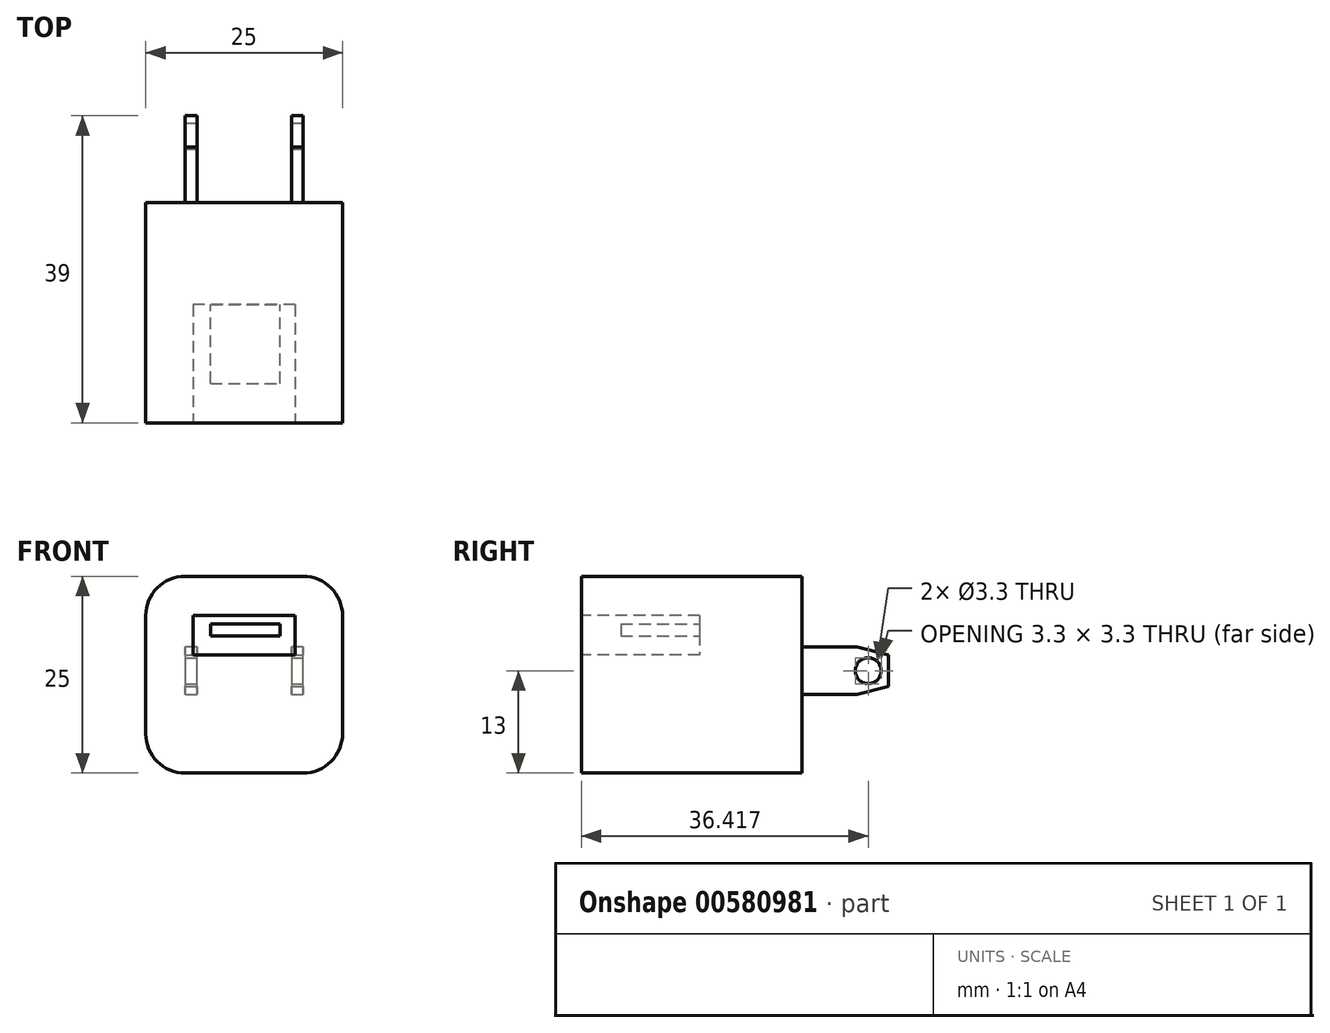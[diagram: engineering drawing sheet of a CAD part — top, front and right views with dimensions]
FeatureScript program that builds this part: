
annotation { "Feature Type Name" : "Feature", "Feature Type Description" : "" }
export const myFeature = defineFeature(function(context is Context, id is Id, definition is map)
    precondition{}
    {
        {
            var Q0;
            Q0=qCreatedBy(makeId("Front.planeOp"),FACE);
            var sketch = newSketch(context, id + "F0", { "sketchPlane" : qUnion([Q0])});
            skLineSegment(sketch, "E0.bottom", {"start": v(12.5, 12.5) * mm, "end": v(-12.5, 12.5) * mm});
            skLineSegment(sketch, "E0.top", {"start": v(12.5, -12.5) * mm, "end": v(-12.5, -12.5) * mm});
            skLineSegment(sketch, "E0.left", {"start": v(12.5, 12.5) * mm, "end": v(12.5, -12.5) * mm});
            skLineSegment(sketch, "E0.right", {"start": v(-12.5, 12.5) * mm, "end": v(-12.5, -12.5) * mm});
            skPoint(sketch, "E0.middle", {"position": v(0, 0) * mm});
            skSolve(sketch);
        }
        {
            var Q0;
            Q0=makeQuery(id+"F0.imprint","IMPRINT",FACE,{"disambiguationData":[TD([[makeQuery(id+"F0.imprint","IMPRINT",EDGE,{"derivedFrom":sQuery(id+"F0.wireOp",EDGE,"E0.bottom")}),1.0]])]});
            extrude(context, id + "F1", {"entities" : qUnion([Q0]), "endBound" : BoundingType.SYMMETRIC, "oppositeDirection" : true, "depth" : 28 * mm, "offsetDistance" : 25 * mm});
        }
        {
            var Q0;
            Q0=makeQuery(id+"F1.opExtrude","CAP_FACE",FACE,{"disambiguationData":[OSD([sQuery(id+"F0.wireOp",EDGE,"E0.bottom"),sQuery(id+"F0.wireOp",EDGE,"E0.top"),sQuery(id+"F0.wireOp",EDGE,"E0.left"),sQuery(id+"F0.wireOp",EDGE,"E0.right")])],"isStart":true});
            var sketch = newSketch(context, id + "F2", { "sketchPlane" : qUnion([Q0])});
            skPoint(sketch, "E1.endSnap0", {"position": v(0, -12.5) * mm});
            skLineSegment(sketch, "E2", {"start": v(0, 2.5) * mm, "end": v(-6.5, 2.5) * mm});
            skLineSegment(sketch, "E3", {"start": v(-6.5, 2.5) * mm, "end": v(-6.5, 7.5) * mm});
            skLineSegment(sketch, "E4", {"start": v(-6.5, 7.5) * mm, "end": v(6.5, 7.5) * mm});
            skLineSegment(sketch, "E5", {"start": v(6.5, 7.5) * mm, "end": v(6.5, 2.5) * mm});
            skLineSegment(sketch, "E6", {"start": v(6.5, 2.5) * mm, "end": v(0, 2.5) * mm});
            skSolve(sketch);
        }
        {
            var Q0;
            Q0=makeQuery(id+"F2.imprint","IMPRINT",FACE,{"disambiguationData":[TD([[makeQuery(id+"F2.imprint","IMPRINT",EDGE,{"derivedFrom":sQuery(id+"F2.wireOp",EDGE,"E2")}),-1.0]])]});
            extrude(context, id + "F3", {"entities" : qUnion([Q0]), "operationType" : NewBodyOperationType.REMOVE, "oppositeDirection" : true, "depth" : 15 * mm, "offsetDistance" : 25 * mm});
        }
        {
            var Q0;
            Q0=makeQuery(id+"F1.opExtrude","CAP_FACE",FACE,{"disambiguationData":[OSD([sQuery(id+"F0.wireOp",EDGE,"E0.bottom"),sQuery(id+"F0.wireOp",EDGE,"E0.top"),sQuery(id+"F0.wireOp",EDGE,"E0.left"),sQuery(id+"F0.wireOp",EDGE,"E0.right")])],"isStart":false});
            var sketch = newSketch(context, id + "F4", { "sketchPlane" : qUnion([Q0])});
            skLineSegment(sketch, "E7", {"start": v(-7.5, -2.5) * mm, "end": v(-7.5, 3.5) * mm});
            skLineSegment(sketch, "E8", {"start": v(-7.5, 3.5) * mm, "end": v(-6, 3.5) * mm});
            skLineSegment(sketch, "E9", {"start": v(-6, 3.5) * mm, "end": v(-6, -2.5) * mm});
            skLineSegment(sketch, "E10", {"start": v(-6, -2.5) * mm, "end": v(-7.5, -2.5) * mm});
            skLineSegment(sketch, "E11", {"start": v(12.5, -12.5) * mm, "end": v(7.5, -12.5) * mm});
            skLineSegment(sketch, "E12", {"start": v(7.5, -2.5) * mm, "end": v(6, -2.5) * mm});
            skLineSegment(sketch, "E13", {"start": v(6, -2.5) * mm, "end": v(6, 3.5) * mm});
            skLineSegment(sketch, "E14", {"start": v(6, 3.5) * mm, "end": v(7.5, 3.5) * mm});
            skLineSegment(sketch, "E15", {"start": v(7.5, 3.5) * mm, "end": v(7.5, -2.5) * mm});
            skSolve(sketch);
        }
        {
            var Q0;
            Q0=makeQuery(id+"F4.imprint","IMPRINT",FACE,{"disambiguationData":[TD([[makeQuery(id+"F4.imprint","IMPRINT",EDGE,{"derivedFrom":sQuery(id+"F4.wireOp",EDGE,"E7")}),-1.0]])]});
            var Q1;
            Q1=makeQuery(id+"F4.imprint","IMPRINT",FACE,{"disambiguationData":[TD([[makeQuery(id+"F4.imprint","IMPRINT",EDGE,{"derivedFrom":sQuery(id+"F4.wireOp",EDGE,"E12")}),-1.0]])]});
            extrude(context, id + "F5", {"entities" : qUnion([Q0, Q1]), "operationType" : NewBodyOperationType.ADD, "depth" : 11 * mm, "offsetDistance" : 25 * mm});
        }
        {
            var Q0;
            Q0=makeQuery(id+"F5.opExtrude","SWEPT_FACE",FACE,{"disambiguationData":[OSD([sQuery(id+"F4.wireOp",EDGE,"E7")])]});
            var sketch = newSketch(context, id + "F6", { "sketchPlane" : qUnion([Q0])});
            skLineSegment(sketch, "E16", {"start": v(25, 3.5) * mm, "end": v(25, 2.5) * mm});
            skLineSegment(sketch, "E17", {"start": v(25, 3.5) * mm, "end": v(21, 3.5) * mm});
            skLineSegment(sketch, "E18", {"start": v(21, 3.5) * mm, "end": v(25, 2.5) * mm});
            skLineSegment(sketch, "E19", {"start": v(25, -2.5) * mm, "end": v(25, -1.5) * mm});
            skLineSegment(sketch, "E20", {"start": v(25, -1.5) * mm, "end": v(21, -2.5) * mm});
            skLineSegment(sketch, "E21", {"start": v(21, -2.5) * mm, "end": v(25, -2.5) * mm});
            skCircle(sketch, "E22", {"center": v(22.42, 0.5) * mm, "radius": 1.65 * mm});
            skSolve(sketch);
        }
        {
            var Q0;
            Q0=makeQuery(id+"F6.imprint","IMPRINT",FACE,{"disambiguationData":[TD([[makeQuery(id+"F6.imprint","IMPRINT",EDGE,{"derivedFrom":sQuery(id+"F6.wireOp",EDGE,"E22")}),1.0]])]});
            var Q1;
            Q1=makeQuery(id+"F6.imprint","IMPRINT",FACE,{"disambiguationData":[TD([[makeQuery(id+"F6.imprint","IMPRINT",EDGE,{"derivedFrom":sQuery(id+"F6.wireOp",EDGE,"E16")}),1.0]])]});
            var Q2;
            Q2=makeQuery(id+"F6.imprint","IMPRINT",FACE,{"disambiguationData":[TD([[makeQuery(id+"F6.imprint","IMPRINT",EDGE,{"derivedFrom":sQuery(id+"F6.wireOp",EDGE,"E19")}),1.0]])]});
            extrude(context, id + "F7", {"entities" : qUnion([Q0, Q1, Q2]), "operationType" : NewBodyOperationType.REMOVE, "oppositeDirection" : true, "depth" : 30.4 * mm, "offsetDistance" : 25 * mm});
        }
        {
            var Q0;
            Q0=makeQuery(id+"F1.opExtrude","SWEPT_EDGE",EDGE,{"disambiguationData":[OSD([sQuery(id+"F0.wireOp",EDGE,"E0.bottom"),sQuery(id+"F0.wireOp",EDGE,"E0.right")])]});
            var Q1;
            Q1=makeQuery(id+"F1.opExtrude","SWEPT_EDGE",EDGE,{"disambiguationData":[OSD([sQuery(id+"F0.wireOp",EDGE,"E0.bottom"),sQuery(id+"F0.wireOp",EDGE,"E0.left")])]});
            var Q2;
            Q2=makeQuery(id+"F1.opExtrude","SWEPT_EDGE",EDGE,{"disambiguationData":[OSD([sQuery(id+"F0.wireOp",EDGE,"E0.top"),sQuery(id+"F0.wireOp",EDGE,"E0.left")])]});
            var Q3;
            Q3=makeQuery(id+"F1.opExtrude","SWEPT_EDGE",EDGE,{"disambiguationData":[OSD([sQuery(id+"F0.wireOp",EDGE,"E0.top"),sQuery(id+"F0.wireOp",EDGE,"E0.right")])]});
            fillet(context, id + "F8", {"entities" : qUnion([Q0, Q1, Q2, Q3]), "radius" : 5 * mm, "tangentPropagation" : true, "allowEdgeOverflow" : false});
        }
        {
            var Q0;
            Q0=makeQuery(id+"F3.boolean.opBoolean","COPY",FACE,{"derivedFrom":makeQuery(id+"F3.opExtrude","CAP_FACE",FACE,{"disambiguationData":[OSD([sQuery(id+"F2.wireOp",EDGE,"E2"),sQuery(id+"F2.wireOp",EDGE,"E3"),sQuery(id+"F2.wireOp",EDGE,"E4"),sQuery(id+"F2.wireOp",EDGE,"E5"),sQuery(id+"F2.wireOp",EDGE,"E6")])],"isStart":false})});
            var sketch = newSketch(context, id + "F9", { "sketchPlane" : qUnion([Q0])});
            skLineSegment(sketch, "E23.bottom", {"start": v(-4.28, 6.44) * mm, "end": v(4.58, 6.44) * mm});
            skLineSegment(sketch, "E23.top", {"start": v(-4.28, 4.93) * mm, "end": v(4.58, 4.93) * mm});
            skLineSegment(sketch, "E23.left", {"start": v(-4.28, 6.44) * mm, "end": v(-4.28, 4.93) * mm});
            skLineSegment(sketch, "E23.right", {"start": v(4.58, 6.44) * mm, "end": v(4.58, 4.93) * mm});
            skSolve(sketch);
        }
        {
            var Q0;
            Q0=makeQuery(id+"F9.imprint","IMPRINT",FACE,{"disambiguationData":[TD([[makeQuery(id+"F9.imprint","IMPRINT",EDGE,{"derivedFrom":sQuery(id+"F9.wireOp",EDGE,"E23.bottom")}),-1.0]])]});
            extrude(context, id + "F10", {"entities" : qUnion([Q0]), "operationType" : NewBodyOperationType.ADD, "depth" : 10 * mm, "offsetDistance" : 25 * mm});
        }
    });
